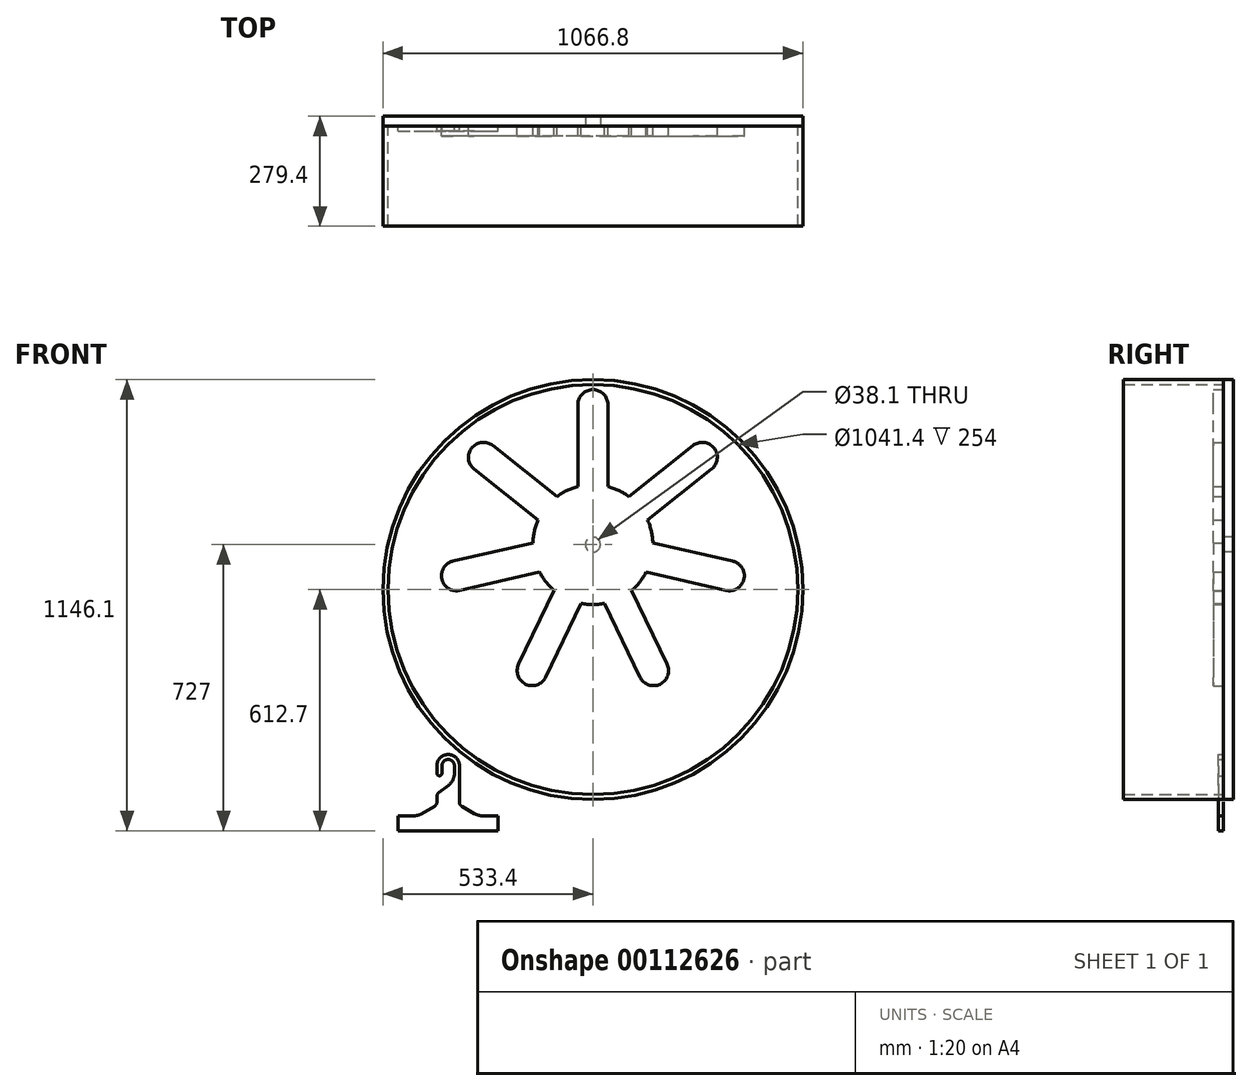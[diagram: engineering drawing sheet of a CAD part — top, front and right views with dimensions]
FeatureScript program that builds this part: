
annotation { "Feature Type Name" : "Feature", "Feature Type Description" : "" }
export const myFeature = defineFeature(function(context is Context, id is Id, definition is map)
    precondition{}
    {
        {
            var Q0;
            Q0=qCreatedBy(makeId("Front.planeOp"),FACE);
            var sketch = newSketch(context, id + "F0", { "sketchPlane" : qUnion([Q0])});
            skArc(sketch, "E0", {"start": v(533.4, 0) * mm, "mid": v(0, 533.4) * mm, "end": v(-533.4, 0) * mm});
            skArc(sketch, "E1.0", {"start": v(520.7, 0) * mm, "mid": v(0, 520.7) * mm, "end": v(-520.7, 0) * mm});
            skLineSegment(sketch, "E2", {"start": v(-533.4, 0) * mm, "end": v(-533.4, 0) * mm});
            skLineSegment(sketch, "E3.0", {"start": v(-520.7, 0) * mm, "end": v(-520.7, 0) * mm});
            skArc(sketch, "E4", {"start": v(-533.4, 0) * mm, "mid": v(0, -533.4) * mm, "end": v(533.4, 0) * mm});
            skArc(sketch, "E5", {"start": v(-520.7, 0) * mm, "mid": v(0, -520.7) * mm, "end": v(520.7, 0) * mm});
            skLineSegment(sketch, "E6", {"start": v(0, 0) * mm, "end": v(0, 0) * mm});
            skLineSegment(sketch, "E7.MirrorCS", {"start": v(520.7, 0) * mm, "end": v(520.7, 0) * mm});
            skLineSegment(sketch, "E8.MirrorCS", {"start": v(533.4, 0) * mm, "end": v(533.4, 0) * mm});
            skSolve(sketch);
        }
        {
            var Q0;
            Q0=qCreatedBy(makeId("Front.planeOp"),FACE);
            var sketch = newSketch(context, id + "F1", { "sketchPlane" : qUnion([Q0])});
            skArc(sketch, "E9", {"start": v(-139.12, 176.51) * mm, "mid": v(-148.58, 148.21) * mm, "end": v(-152.34, 118.6) * mm});
            skLineSegment(sketch, "E10", {"start": v(0, 266.7) * mm, "end": v(0, 469.9) * mm, "construction": true});
            skLineSegment(sketch, "E11.0", {"start": v(-38.1, 261.86) * mm, "end": v(-38.1, 469.9) * mm});
            skLineSegment(sketch, "E12.0", {"start": v(38.1, 261.86) * mm, "end": v(38.1, 469.9) * mm});
            skArc(sketch, "E13", {"start": v(38.1, 469.9) * mm, "mid": v(0, 508) * mm, "end": v(-38.1, 469.9) * mm});
            skArc(sketch, "E14.1.0", {"start": v(-254.26, 365.8) * mm, "mid": v(-307.8, 359.77) * mm, "end": v(-301.77, 306.23) * mm});
            skLineSegment(sketch, "E14.1.1", {"start": v(-139.12, 176.51) * mm, "end": v(-301.77, 306.23) * mm});
            skLineSegment(sketch, "E14.1.2", {"start": v(-91.61, 236.1) * mm, "end": v(-254.26, 365.8) * mm});
            skArc(sketch, "E14.2.0", {"start": v(-355.16, 72.32) * mm, "mid": v(-383.83, 26.7) * mm, "end": v(-338.2, -1.97) * mm});
            skLineSegment(sketch, "E14.2.1", {"start": v(-135.38, 44.32) * mm, "end": v(-338.2, -1.97) * mm});
            skLineSegment(sketch, "E14.2.2", {"start": v(-152.34, 118.6) * mm, "end": v(-355.16, 72.32) * mm});
            skArc(sketch, "E15.3.3.0", {"start": v(-188.62, -189.55) * mm, "mid": v(-170.82, -240.41) * mm, "end": v(-119.96, -222.62) * mm});
            skLineSegment(sketch, "E15.4.3.0", {"start": v(-29.7, -35.18) * mm, "end": v(-119.96, -222.62) * mm});
            skLineSegment(sketch, "E15.7.3.0", {"start": v(-98.35, -2.12) * mm, "end": v(-188.62, -189.55) * mm});
            skArc(sketch, "E15.3.4.0", {"start": v(119.96, -222.62) * mm, "mid": v(170.82, -240.41) * mm, "end": v(188.62, -189.55) * mm});
            skLineSegment(sketch, "E15.4.4.0", {"start": v(98.35, -2.12) * mm, "end": v(188.62, -189.55) * mm});
            skLineSegment(sketch, "E15.7.4.0", {"start": v(29.7, -35.18) * mm, "end": v(119.96, -222.62) * mm});
            skArc(sketch, "E15.3.5.0", {"start": v(338.2, -1.97) * mm, "mid": v(383.83, 26.7) * mm, "end": v(355.16, 72.32) * mm});
            skLineSegment(sketch, "E15.4.5.0", {"start": v(152.34, 118.6) * mm, "end": v(355.16, 72.32) * mm});
            skLineSegment(sketch, "E15.7.5.0", {"start": v(135.38, 44.32) * mm, "end": v(338.2, -1.97) * mm});
            skArc(sketch, "E16.trimOffspring", {"start": v(91.61, 236.1) * mm, "mid": v(66.12, 251.6) * mm, "end": v(38.1, 261.86) * mm});
            skArc(sketch, "E17.trimOffspring", {"start": v(-29.7, -35.18) * mm, "mid": v(0, -38.1) * mm, "end": v(29.7, -35.18) * mm});
            skArc(sketch, "E18.trimOffspring", {"start": v(-135.38, 44.32) * mm, "mid": v(-119.15, 19.28) * mm, "end": v(-98.35, -2.12) * mm});
            skArc(sketch, "E19.trimOffspring", {"start": v(-38.1, 261.86) * mm, "mid": v(-66.12, 251.6) * mm, "end": v(-91.61, 236.1) * mm});
            skArc(sketch, "E20.trimOffspring", {"start": v(98.35, -2.12) * mm, "mid": v(119.15, 19.28) * mm, "end": v(135.38, 44.32) * mm});
            skArc(sketch, "E21.3.6.0", {"start": v(301.77, 306.23) * mm, "mid": v(307.8, 359.77) * mm, "end": v(254.26, 365.8) * mm});
            skLineSegment(sketch, "E21.4.6.0", {"start": v(91.61, 236.1) * mm, "end": v(254.26, 365.8) * mm});
            skLineSegment(sketch, "E21.7.6.0", {"start": v(139.12, 176.51) * mm, "end": v(301.77, 306.23) * mm});
            skArc(sketch, "E22.trimOffspring", {"start": v(152.34, 118.6) * mm, "mid": v(148.58, 148.21) * mm, "end": v(139.12, 176.51) * mm});
            skSolve(sketch);
        }
        {
            var Q0;
            Q0=makeQuery(id+"F0.imprint","IMPRINT",FACE,{"disambiguationData":[TD([[makeQuery(id+"F0.imprint","IMPRINT",EDGE,{"derivedFrom":sQuery(id+"F0.wireOp",EDGE,"E0")}),1.0]])]});
            extrude(context, id + "F2", {"entities" : qUnion([Q0]), "depth" : 254 * mm});
        }
        {
            var Q0;
            Q0=makeQuery(id+"F1.imprint","IMPRINT",FACE,{"disambiguationData":[TD([[makeQuery(id+"F1.imprint","IMPRINT",EDGE,{"derivedFrom":sQuery(id+"F1.wireOp",EDGE,"E9")}),1.0]])]});
            extrude(context, id + "F3", {"entities" : qUnion([Q0]), "depth" : 25.4 * mm});
        }
        {
            var Q0;
            Q0=qCreatedBy(makeId("Front.planeOp"),FACE);
            var sketch = newSketch(context, id + "F4", { "sketchPlane" : qUnion([Q0])});
            skCircle(sketch, "E23.0", {"center": v(0, 0) * mm, "radius": 533.4 * mm});
            skPoint(sketch, "E24.0", {"position": v(0, 114.3) * mm});
            skCircle(sketch, "E25", {"center": v(0, 114.3) * mm, "radius": 19.05 * mm});
            skSolve(sketch);
        }
        {
            var Q0;
            Q0=makeQuery(id+"F4.imprint","IMPRINT",FACE,{"disambiguationData":[TD([[makeQuery(id+"F4.imprint","IMPRINT",EDGE,{"derivedFrom":sQuery(id+"F4.wireOp",EDGE,"E23.0")}),1.0]])]});
            extrude(context, id + "F5", {"entities" : qUnion([Q0]), "oppositeDirection" : true, "depth" : 25.4 * mm});
        }
        {
            var Q0;
            Q0=qCreatedBy(makeId("Front.planeOp"),FACE);
            var sketch = newSketch(context, id + "F6", { "sketchPlane" : qUnion([Q0])});
            skArc(sketch, "E26", {"start": v(-351.82, -447.6) * mm, "mid": v(-367.7, -431.72) * mm, "end": v(-383.57, -447.6) * mm});
            skLineSegment(sketch, "E27", {"start": v(-383.57, -447.6) * mm, "end": v(-383.57, -466.65) * mm});
            skLineSegment(sketch, "E28", {"start": v(-396.27, -447.6) * mm, "end": v(-396.27, -466.65) * mm});
            skArc(sketch, "E29", {"start": v(-396.27, -466.65) * mm, "mid": v(-389.92, -473) * mm, "end": v(-383.57, -466.65) * mm});
            skLineSegment(sketch, "E30", {"start": v(-351.82, -447.6) * mm, "end": v(-351.82, -466.65) * mm});
            skLineSegment(sketch, "E31", {"start": v(-339.12, -447.6) * mm, "end": v(-339.12, -539.77) * mm});
            skLineSegment(sketch, "E32", {"start": v(-367.7, -447.6) * mm, "end": v(-367.7, -478.08) * mm, "construction": true});
            skArc(sketch, "E33", {"start": v(-366.99, -497.07) * mm, "mid": v(-355.82, -483.65) * mm, "end": v(-351.82, -466.65) * mm});
            skLineSegment(sketch, "E34", {"start": v(-366.99, -497.07) * mm, "end": v(-391.21, -515.33) * mm});
            skLineSegment(sketch, "E35", {"start": v(-367.7, -447.6) * mm, "end": v(-367.7, -612.7) * mm, "construction": true});
            skLineSegment(sketch, "E36", {"start": v(-494.7, -612.7) * mm, "end": v(-240.7, -612.7) * mm});
            skLineSegment(sketch, "E37.trimOffspring", {"start": v(-396.27, -525.48) * mm, "end": v(-396.27, -539.77) * mm});
            skPoint(sketch, "E38.visualSharp", {"position": v(-396.27, -519.14) * mm});
            skArc(sketch, "E38.filletArc", {"start": v(-391.21, -515.33) * mm, "mid": v(-394.94, -519.8) * mm, "end": v(-396.27, -525.48) * mm});
            skLineSegment(sketch, "E39.0", {"start": v(-494.7, -574.6) * mm, "end": v(-454.1, -574.6) * mm});
            skLineSegment(sketch, "E40", {"start": v(-494.7, -574.6) * mm, "end": v(-494.7, -612.7) * mm});
            skLineSegment(sketch, "E41", {"start": v(-240.7, -574.6) * mm, "end": v(-240.7, -612.7) * mm});
            skLineSegment(sketch, "E42", {"start": v(-435.05, -569.5) * mm, "end": v(-402.62, -550.77) * mm});
            skLineSegment(sketch, "E43.MirrorCS", {"start": v(-300.34, -569.5) * mm, "end": v(-332.77, -550.77) * mm});
            skLineSegment(sketch, "E44.trimOffspring", {"start": v(-281.29, -574.6) * mm, "end": v(-240.7, -574.6) * mm});
            skPoint(sketch, "E45.visualSharp", {"position": v(-396.27, -547.1) * mm});
            skArc(sketch, "E45.filletArc", {"start": v(-402.62, -550.77) * mm, "mid": v(-397.97, -546.12) * mm, "end": v(-396.27, -539.77) * mm});
            skPoint(sketch, "E46.visualSharp", {"position": v(-339.12, -547.1) * mm});
            skArc(sketch, "E46.filletArc", {"start": v(-339.12, -539.77) * mm, "mid": v(-337.42, -546.12) * mm, "end": v(-332.77, -550.77) * mm});
            skPoint(sketch, "E47.visualSharp", {"position": v(-443.9, -574.6) * mm});
            skArc(sketch, "E47.filletArc", {"start": v(-454.1, -574.6) * mm, "mid": v(-444.24, -573.3) * mm, "end": v(-435.05, -569.5) * mm});
            skPoint(sketch, "E48.visualSharp", {"position": v(-291.5, -574.6) * mm});
            skArc(sketch, "E48.filletArc", {"start": v(-300.34, -569.5) * mm, "mid": v(-291.15, -573.3) * mm, "end": v(-281.29, -574.6) * mm});
            skArc(sketch, "E49.trimOffspring", {"start": v(-339.12, -447.6) * mm, "mid": v(-367.7, -419.02) * mm, "end": v(-396.27, -447.6) * mm});
            skLineSegment(sketch, "E50", {"start": v(-383.57, -447.6) * mm, "end": v(-351.82, -447.6) * mm, "construction": true});
            skSolve(sketch);
        }
        {
            var Q0;
            Q0=makeQuery(id+"F6.imprint","IMPRINT",FACE,{"disambiguationData":[TD([[makeQuery(id+"F6.imprint","IMPRINT",EDGE,{"derivedFrom":sQuery(id+"F6.wireOp",EDGE,"E26")}),-1.0]])]});
            extrude(context, id + "F7", {"entities" : qUnion([Q0]), "depth" : 12.7 * mm});
        }
    });
